# Revit family: Блок упора Б-9а 730x800x250h
name_source: partatom
category: Обобщенные модели
units: mm (PartAtom-declared; Revit-internal decimal feet)

## family parameters
Всегда вертикально = Да
Может служить основой для арматурных стержней = Нет
На основе рабочей плоскости = Нет
Общий = Нет
При загрузке вырезать с полостями = Нет
Размер круглого соединителя = Использовать диаметр
Сохранять ориентацию аннотаций = Нет
Тип детали = Нормальный
Точка принадлежности помещению = Нет

## types (1)
- Блок упора Б-9а 730x800x250h
    ADSK_Размер_Длина = 800 мм
    ADSK_Размер_Толщина = 250 мм
    ADSK_Размер_Ширина = 730 мм
    Глубина переднего выреза = 150 мм
    Отметка по умолчанию = 0 мм
    Отступ петли = 125 мм
    Отступ петли от края блока = 200 мм
    Смещение выреза от верха = 12 мм
    Толщина низкого края = 150 мм
    Ширина переднего выреза = 530 мм
    Ширина полки = 627 мм
    высота_петли = 70 мм
    скос боковой грани = 2 мм
    скос внутренней передней грани = 3 мм
    скос передней грани = 1 мм
    фаска = 40 мм
    ширина_петли = 70 мм
